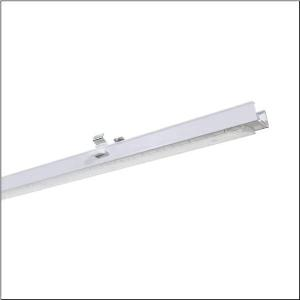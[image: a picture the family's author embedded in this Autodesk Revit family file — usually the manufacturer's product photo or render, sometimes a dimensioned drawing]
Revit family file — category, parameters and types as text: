
# Revit family: trunking_flex_31_51re12ma66b
name_source: partatom
category: Lighting Fixtures
units: mm (PartAtom-declared; Revit-internal decimal feet)

## family parameters
Cut with Voids When Loaded = No
Host = Face
Light Source = No
Part Type = Normal
Room Calculation Point = No
Round Connector Dimension = Use Diameter
Shared = No

## types (1)
- --- (1 x LED, 6400 lm, 40 W, 6500K)
    Apparent Load = 40 VA
    CIE Flux Codes = 65 91 98 99 100
    Color Rendering = 80
    Color Temperature = 6500K
    Default Elevation = 1800 mm
    Description = Trunking Flex 31, luminaire insert, of extruded aluminium section, coated, traffic white (RAL 9016), length: 1.172mm, width: 91mm, height: 53mm, LED rated luminous flux: 6.400lm, light colour: 865, SDCM (Standard Deviation of Colour Matching)MacAdam ≤ 3 SDCM (initial), control gear: ON/OFF Multilumen, with system connector: socket, mains connection: 220..240V, AC, 50/60Hz, rated input power: 40W, luminous flux adjustable on luminaire in four steps (3420/4540/5580/6630lm), connected load according to luminous flux setting (20/26/33/40W), primary light control with lens, of plastic, primary optical cover: cover, of PMMA, light emission: direct distribution, protection rating (complete): IP20, insulation class (complete): insulation class I (protective earthing), certification: CE, UKCA, impact resistance: IK02, permissible ambient temperature for indoor applications: -20..+40°C, packaging unit: 1 piece
    Height = 58 mm
    Lamp = 1 x LED
    Lamp Light Flux = 6400 lm
    Lamp Power = 40 W
    Lamp count = 1
    Length = 1172 mm
    Luminous efficacy = 160 lm/W
    Manufacturer = Siteco
    ModVariant = No
    Model = 51RE12MA66B
    Mounting Place = Ceiling
    Mounting Type = Pendant
    Number of Poles = 1
    OnlyDefault = Yes
    Power Factor = 1
    Product Name = Trunking Flex 31
    Product group = luminaire insert | ceiling pendant
    ProductGroupID = 901
    Protection Class = Protection class I
    Protection Degree = IP 20
    RLX_Detail_Level = 1
    RLX_Emergency_Light_Flux = 0 lm
    RLX_Emergency_Type = 0
    RLX_Emergency_Type_DB = No
    RlxData = <blob elided: 20065 chars, md5=7712eac2>
    Socket = socket
    Standby Power = 0 W
    System Light Flux = 6400 lm
    System Power = 40 W
    Type Comments = factory setting: luminous flux: 100 % | (ON | ON) | 300 mA
    Type Image = l_1266702.jpg
    URL = http://relux.com
    VarID = @adj_067123
    Voltage = 0 V
    Weight = 0.00 kg
    Width = 65 mm

## geometry (parser evidence)
native form markers: Blend x4, Sweep x10
no freeform markers — native parametric forms only
